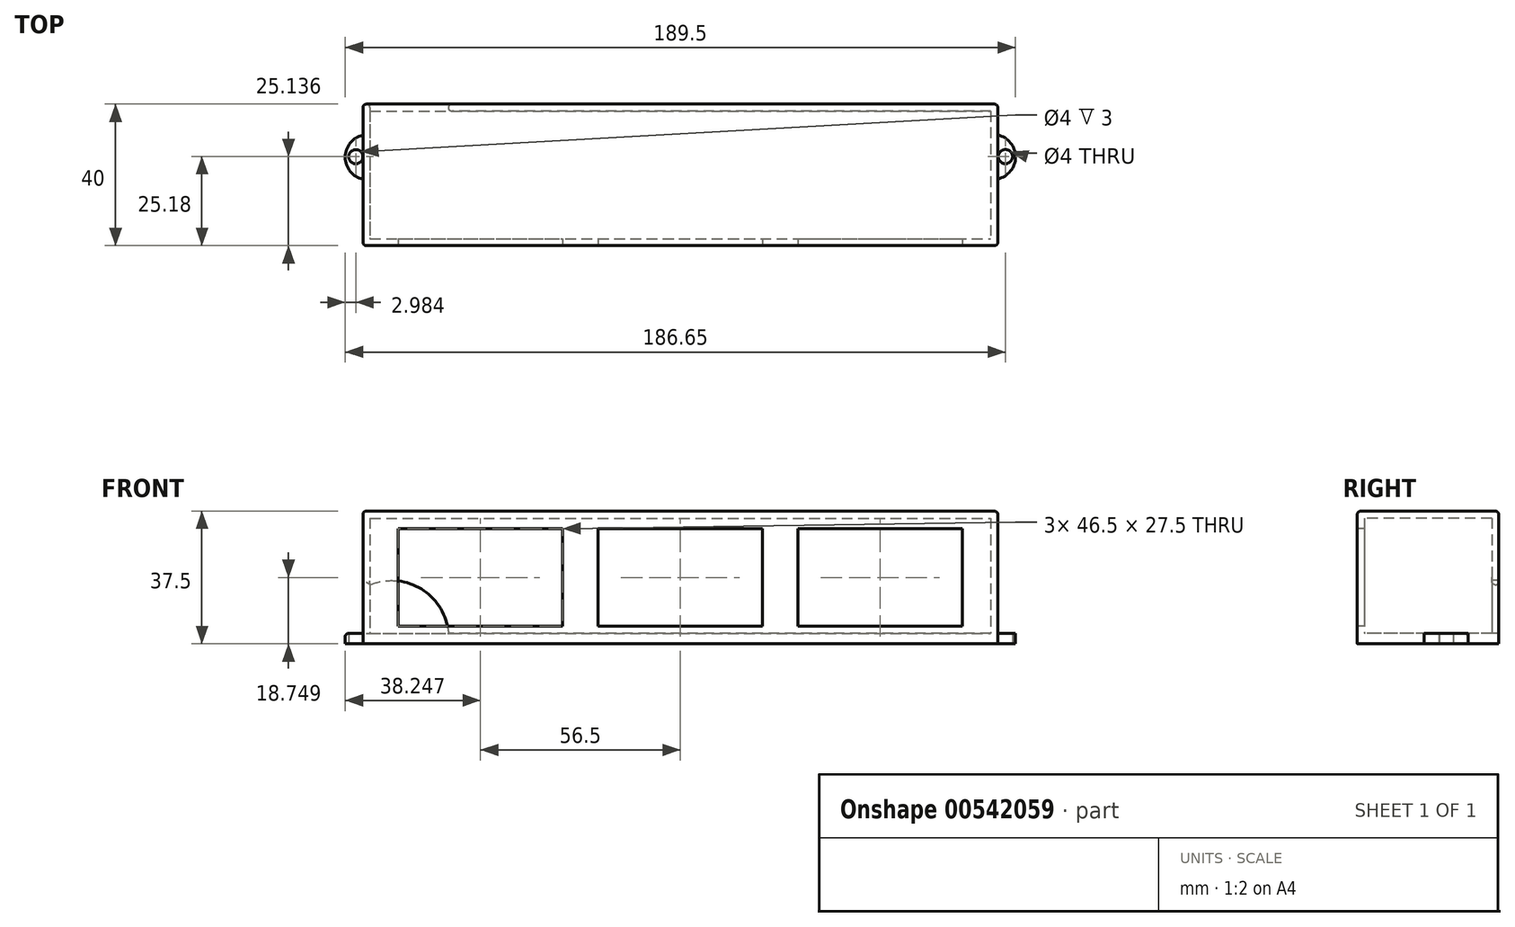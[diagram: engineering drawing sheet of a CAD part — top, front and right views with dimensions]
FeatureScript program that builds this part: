
annotation { "Feature Type Name" : "Feature", "Feature Type Description" : "" }
export const myFeature = defineFeature(function(context is Context, id is Id, definition is map)
    precondition{}
    {
        {
            var Q0;
            Q0=qCreatedBy(makeId("Front.planeOp"),FACE);
            var sketch = newSketch(context, id + "F0", { "sketchPlane" : qUnion([Q0])});
            skLineSegment(sketch, "E0.bottom", {"start": v(-100.51, 9.59) * mm, "end": v(78.99, 9.59) * mm});
            skLineSegment(sketch, "E0.top", {"start": v(-100.51, -27.91) * mm, "end": v(78.99, -27.91) * mm});
            skLineSegment(sketch, "E0.left", {"start": v(-100.51, 9.59) * mm, "end": v(-100.51, -27.91) * mm});
            skLineSegment(sketch, "E0.right", {"start": v(78.99, 9.59) * mm, "end": v(78.99, -27.91) * mm});
            skLineSegment(sketch, "E1.bottom", {"start": v(-90.51, 4.59) * mm, "end": v(-44.01, 4.59) * mm});
            skLineSegment(sketch, "E1.top", {"start": v(-90.51, -22.91) * mm, "end": v(-44.01, -22.91) * mm});
            skLineSegment(sketch, "E1.left", {"start": v(-90.51, 4.59) * mm, "end": v(-90.51, -22.91) * mm});
            skLineSegment(sketch, "E1.right", {"start": v(-44.01, 4.59) * mm, "end": v(-44.01, -22.91) * mm});
            skLineSegment(sketch, "E2.bottom", {"start": v(-34.01, 4.59) * mm, "end": v(12.49, 4.59) * mm});
            skLineSegment(sketch, "E2.top", {"start": v(-34.01, -22.91) * mm, "end": v(12.49, -22.91) * mm});
            skLineSegment(sketch, "E2.left", {"start": v(-34.01, 4.59) * mm, "end": v(-34.01, -22.91) * mm});
            skLineSegment(sketch, "E2.right", {"start": v(12.49, 4.59) * mm, "end": v(12.49, -22.91) * mm});
            skLineSegment(sketch, "E3.bottom", {"start": v(22.49, 4.59) * mm, "end": v(68.99, 4.59) * mm});
            skLineSegment(sketch, "E3.top", {"start": v(22.49, -22.91) * mm, "end": v(68.99, -22.91) * mm});
            skLineSegment(sketch, "E3.left", {"start": v(22.49, 4.59) * mm, "end": v(22.49, -22.91) * mm});
            skLineSegment(sketch, "E3.right", {"start": v(68.99, 4.59) * mm, "end": v(68.99, -22.91) * mm});
            skLineSegment(sketch, "E4.0", {"start": v(-98.51, 7.59) * mm, "end": v(76.99, 7.59) * mm});
            skLineSegment(sketch, "E4.1", {"start": v(-98.51, 7.59) * mm, "end": v(-98.51, -25.91) * mm});
            skLineSegment(sketch, "E4.2", {"start": v(-98.51, -25.91) * mm, "end": v(76.99, -25.91) * mm});
            skLineSegment(sketch, "E4.3", {"start": v(76.99, 7.59) * mm, "end": v(76.99, -25.91) * mm});
            skSolve(sketch);
        }
        {
            var Q0;
            Q0 = qSketchRegion(id + "F0", true);
            extrude(context, id + "F1", {"entities" : qUnion([Q0]), "oppositeDirection" : true, "depth" : 40 * mm, "offsetDistance" : 25 * mm});
        }
        {
            var Q0;
            Q0=makeQuery(id+"F0.imprint","IMPRINT",FACE,{"disambiguationData":[TD([[makeQuery(id+"F0.imprint","IMPRINT",EDGE,{"derivedFrom":sQuery(id+"F0.wireOp",EDGE,"E1.bottom")}),1.0]])]});
            extrude(context, id + "F2", {"entities" : qUnion([Q0]), "operationType" : NewBodyOperationType.ADD, "oppositeDirection" : true, "depth" : 2 * mm, "offsetDistance" : 25 * mm});
        }
        {
            var Q0;
            Q0=makeQuery(id+"F1.opExtrude","CAP_FACE",FACE,{"disambiguationData":[OSD([sQuery(id+"F0.wireOp",EDGE,"E0.bottom"),sQuery(id+"F0.wireOp",EDGE,"E0.top"),sQuery(id+"F0.wireOp",EDGE,"E0.left"),sQuery(id+"F0.wireOp",EDGE,"E0.right"),sQuery(id+"F0.wireOp",EDGE,"E4.0"),sQuery(id+"F0.wireOp",EDGE,"E4.1"),sQuery(id+"F0.wireOp",EDGE,"E4.2"),sQuery(id+"F0.wireOp",EDGE,"E4.3")])],"isStart":false});
            var sketch = newSketch(context, id + "F3", { "sketchPlane" : qUnion([Q0])});
            skLineSegment(sketch, "E5.bottom", {"start": v(-76.99, 7.59) * mm, "end": v(98.51, 7.59) * mm});
            skLineSegment(sketch, "E5.top", {"start": v(-76.99, -25.91) * mm, "end": v(98.51, -25.91) * mm});
            skLineSegment(sketch, "E5.left", {"start": v(-76.99, 7.59) * mm, "end": v(-76.99, -25.91) * mm});
            skLineSegment(sketch, "E5.right", {"start": v(98.51, 7.59) * mm, "end": v(98.51, -25.91) * mm});
            skArc(sketch, "E6", {"start": v(98.51, -11.23) * mm, "mid": v(83.53, -12.71) * mm, "end": v(76.29, -25.91) * mm});
            skSolve(sketch);
        }
        {
            var Q0;
            {var subQ1=sQuery(id+"F3.wireOp",EDGE,"E5.bottom");Q0=makeQuery(id+"F3.imprint","IMPRINT",FACE,{"disambiguationData":[TD([[makeQuery(id+"F3.imprint","IMPRINT",EDGE,{"derivedFrom":subQ1}),1.0]])]});}
            extrude(context, id + "F4", {"entities" : qUnion([Q0]), "operationType" : NewBodyOperationType.ADD, "oppositeDirection" : true, "depth" : 2 * mm, "offsetDistance" : 25 * mm});
        }
        {
            var Q0;
            Q0=makeQuery(id+"F1.opExtrude","SWEPT_FACE",FACE,{"disambiguationData":[OSD([sQuery(id+"F0.wireOp",EDGE,"E0.top")])]});
            var sketch = newSketch(context, id + "F5", { "sketchPlane" : qUnion([Q0])});
            skArc(sketch, "E7", {"start": v(-100.51, -18.77) * mm, "mid": v(-105.51, -25) * mm, "end": v(-100.51, -31.23) * mm});
            skCircle(sketch, "E8", {"center": v(-102.53, -25.14) * mm, "radius": 2 * mm});
            skArc(sketch, "E9", {"start": v(78.99, -31.3) * mm, "mid": v(83.99, -25.06) * mm, "end": v(78.99, -18.83) * mm});
            skCircle(sketch, "E10", {"center": v(81.14, -25.18) * mm, "radius": 2 * mm});
            skSolve(sketch);
        }
        {
            var Q0;
            {var subQ0=sQuery(id+"F5.wireOp",EDGE,"E7");Q0=makeQuery(id+"F5.imprint","IMPRINT",FACE,{"disambiguationData":[TD([[makeQuery(id+"F5.imprint","IMPRINT",EDGE,{"derivedFrom":subQ0}),1.0]])]});}
            extrude(context, id + "F6", {"entities" : qUnion([Q0]), "operationType" : NewBodyOperationType.ADD, "oppositeDirection" : true, "depth" : 3 * mm, "offsetDistance" : 25 * mm});
        }
        {
            var Q0;
            {var subQ0=sQuery(id+"F5.wireOp",EDGE,"E9");Q0=makeQuery(id+"F5.imprint","IMPRINT",FACE,{"disambiguationData":[TD([[makeQuery(id+"F5.imprint","IMPRINT",EDGE,{"derivedFrom":subQ0}),1.0]])]});}
            extrude(context, id + "F7", {"entities" : qUnion([Q0]), "operationType" : NewBodyOperationType.ADD, "oppositeDirection" : true, "depth" : 3 * mm, "offsetDistance" : 25 * mm});
        }
        {
            var Q0;
            Q0=makeQuery(id+"F1.opExtrude","SWEPT_EDGE",EDGE,{"disambiguationData":[OSD([sQuery(id+"F0.wireOp",EDGE,"E0.bottom"),sQuery(id+"F0.wireOp",EDGE,"E0.left")])]});
            fillet(context, id + "F8", {"entities" : qUnion([Q0]), "radius" : 1 * mm, "tangentPropagation" : true, "allowEdgeOverflow" : false});
        }
        {
            var Q0;
            Q0=makeQuery(id+"F1.opExtrude","SWEPT_EDGE",EDGE,{"disambiguationData":[OSD([sQuery(id+"F0.wireOp",EDGE,"E0.bottom"),sQuery(id+"F0.wireOp",EDGE,"E0.right")])]});
            fillet(context, id + "F9", {"entities" : qUnion([Q0]), "radius" : 1 * mm, "tangentPropagation" : true, "allowEdgeOverflow" : false});
        }
        {
            var Q0;
            Q0=makeQuery(id+"F1.opExtrude","CAP_EDGE",EDGE,{"disambiguationData":[OSD([sQuery(id+"F0.wireOp",EDGE,"E0.bottom")])],"isStart":true});
            var Q1;
            Q1=makeQuery(id+"F1.opExtrude","CAP_EDGE",EDGE,{"disambiguationData":[OSD([sQuery(id+"F0.wireOp",EDGE,"E0.right")])],"isStart":false});
            var Q2;
            Q2=makeQuery(id+"F1.opExtrude","CAP_EDGE",EDGE,{"disambiguationData":[OSD([sQuery(id+"F0.wireOp",EDGE,"E0.bottom")])],"isStart":false});
            var Q3;
            Q3=makeQuery(id+"F4.opExtrude","CAP_EDGE",EDGE,{"disambiguationData":[OSD([sQuery(id+"F3.wireOp",EDGE,"E6")])],"isStart":true});
            var Q4;
            Q4=makeQuery(id+"F1.opExtrude","CAP_EDGE",EDGE,{"disambiguationData":[OSD([sQuery(id+"F0.wireOp",EDGE,"E4.1")])],"isStart":false});
            var Q5;
            Q5=makeQuery(id+"F4.opExtrude","CAP_EDGE",EDGE,{"disambiguationData":[OSD([sQuery(id+"F3.wireOp",EDGE,"E6")])],"isStart":false});
            var Q6;
            Q6=makeQuery(id+"F1.opExtrude","CAP_EDGE",EDGE,{"disambiguationData":[OSD([sQuery(id+"F0.wireOp",EDGE,"E4.2")])],"isStart":false});
            var Q7;
            Q7=makeQuery(id+"F6.opExtrude","CAP_EDGE",EDGE,{"disambiguationData":[OSD([sQuery(id+"F5.wireOp",EDGE,"E7")])],"isStart":false});
            var Q8;
            Q8=makeQuery(id+"F7.opExtrude","CAP_EDGE",EDGE,{"disambiguationData":[OSD([sQuery(id+"F5.wireOp",EDGE,"E9")])],"isStart":false});
            fillet(context, id + "F10", {"entities" : qUnion([Q0, Q1, Q2, Q3, Q4, Q5, Q6, Q7, Q8]), "radius" : 1 * mm, "tangentPropagation" : true, "allowEdgeOverflow" : false});
        }
    });
